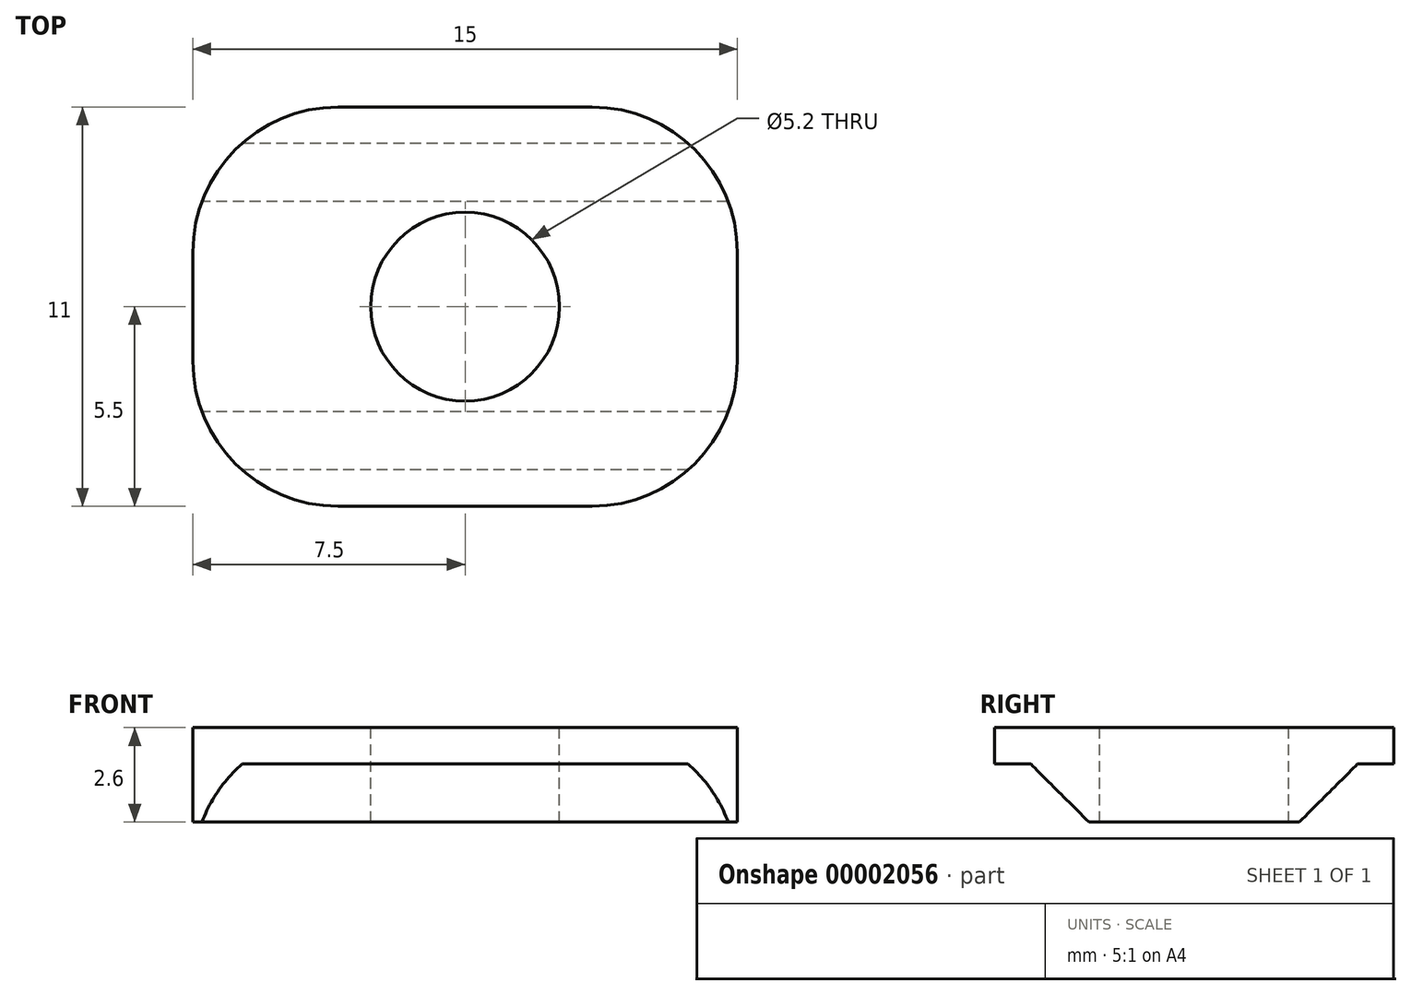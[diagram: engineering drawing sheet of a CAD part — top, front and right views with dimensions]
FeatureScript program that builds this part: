
annotation { "Feature Type Name" : "Feature", "Feature Type Description" : "" }
export const myFeature = defineFeature(function(context is Context, id is Id, definition is map)
    precondition{}
    {
        {
            var Q0;
            Q0=qCreatedBy(makeId("Right.planeOp"),FACE);
            var sketch = newSketch(context, id + "F0", { "sketchPlane" : qUnion([Q0])});
            skLineSegment(sketch, "E0", {"start": v(-5.5, 0) * mm, "end": v(5.5, 0) * mm});
            skLineSegment(sketch, "E1", {"start": v(5.5, 0) * mm, "end": v(5.5, -1) * mm});
            skLineSegment(sketch, "E2", {"start": v(5.5, -1) * mm, "end": v(4.5, -1) * mm});
            skLineSegment(sketch, "E3", {"start": v(4.5, -1) * mm, "end": v(2.9, -2.6) * mm});
            skLineSegment(sketch, "E4", {"start": v(2.9, -2.6) * mm, "end": v(-2.9, -2.6) * mm});
            skLineSegment(sketch, "E5", {"start": v(-2.9, -2.6) * mm, "end": v(-4.5, -1) * mm});
            skLineSegment(sketch, "E6", {"start": v(-4.5, -1) * mm, "end": v(-5.5, -1) * mm});
            skLineSegment(sketch, "E7", {"start": v(-5.5, -1) * mm, "end": v(-5.5, 0) * mm});
            skPoint(sketch, "E8", {"position": v(0, 0) * mm});
            skSolve(sketch);
        }
        {
            var Q0;
            Q0 = qSketchRegion(id + "F0", true);
            extrude(context, id + "F1", {"entities" : qUnion([Q0]), "depth" : 15 * mm});
        }
        {
            var Q0;
            Q0=makeQuery(id+"F1.opExtrude","SWEPT_FACE",FACE,{"disambiguationData":[OSD([sQuery(id+"F0.wireOp",EDGE,"E0")])]});
            var sketch = newSketch(context, id + "F2", { "sketchPlane" : qUnion([Q0])});
            skCircle(sketch, "E9", {"center": v(7.5, 0) * mm, "radius": 2.6 * mm});
            skPoint(sketch, "E10", {"position": v(7.5, 5.5) * mm});
            skSolve(sketch);
        }
        {
            var Q0;
            Q0=makeQuery(id+"F1.opExtrude","CAP_EDGE",EDGE,{"disambiguationData":[OSD([sQuery(id+"F0.wireOp",EDGE,"E7")])],"isStart":false});
            var Q1;
            Q1=makeQuery(id+"F1.opExtrude","CAP_EDGE",EDGE,{"disambiguationData":[OSD([sQuery(id+"F0.wireOp",EDGE,"E1")])],"isStart":false});
            var Q2;
            Q2=makeQuery(id+"F1.opExtrude","CAP_EDGE",EDGE,{"disambiguationData":[OSD([sQuery(id+"F0.wireOp",EDGE,"E7")])],"isStart":true});
            var Q3;
            Q3=makeQuery(id+"F1.opExtrude","CAP_EDGE",EDGE,{"disambiguationData":[OSD([sQuery(id+"F0.wireOp",EDGE,"E1")])],"isStart":true});
            fillet(context, id + "F3", {"entities" : qUnion([Q0, Q1, Q2, Q3]), "radius" : 4 * mm, "tangentPropagation" : true, "allowEdgeOverflow" : false});
        }
        {
            var Q0;
            Q0 = qSketchRegion(id + "F2", true);
            extrude(context, id + "F4", {"entities" : qUnion([Q0]), "operationType" : NewBodyOperationType.REMOVE, "endBound" : BoundingType.THROUGH_ALL, "oppositeDirection" : true, "depth" : 25 * mm});
        }
    });
